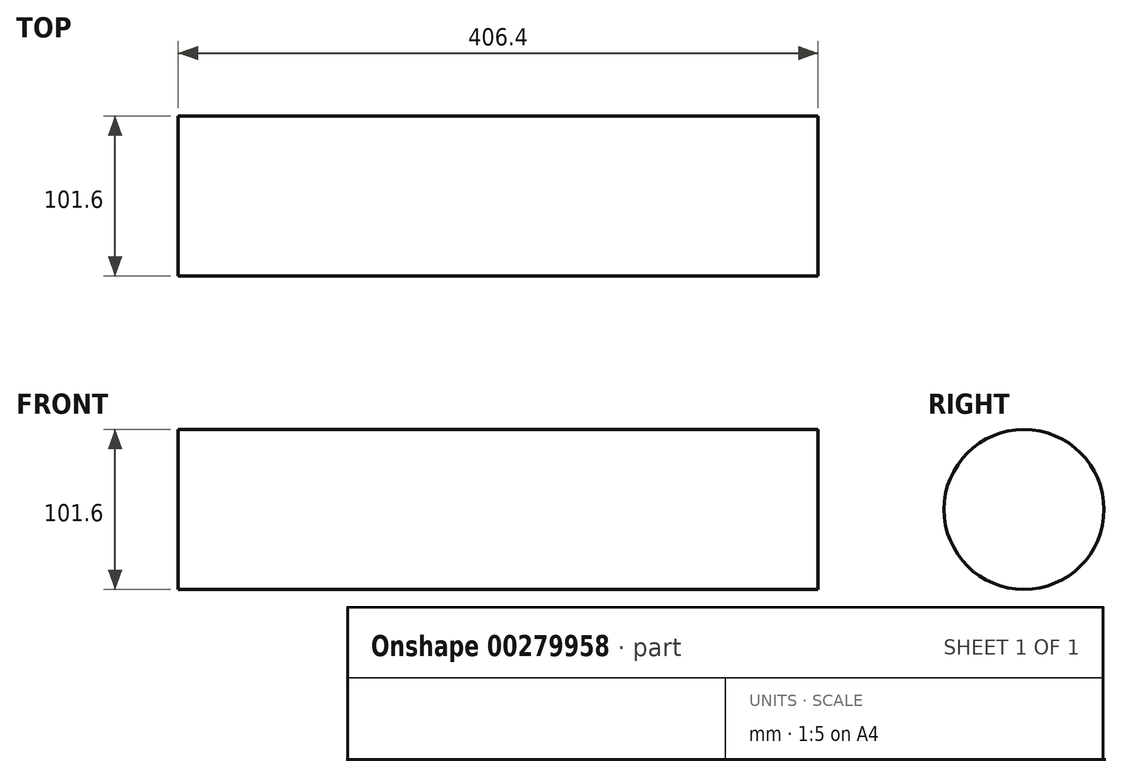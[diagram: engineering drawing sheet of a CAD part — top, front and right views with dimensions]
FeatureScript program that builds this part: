
annotation { "Feature Type Name" : "Feature", "Feature Type Description" : "" }
export const myFeature = defineFeature(function(context is Context, id is Id, definition is map)
    precondition{}
    {
        {
            var Q0;
            Q0=qCreatedBy(makeId("Right.planeOp"),FACE);
            var sketch = newSketch(context, id + "F0", { "sketchPlane" : qUnion([Q0])});
            skCircle(sketch, "E0", {"center": v(0, 0) * mm, "radius": 50.8 * mm});
            skSolve(sketch);
        }
        {
            var Q0;
            Q0=makeQuery(id+"F0.imprint","IMPRINT",FACE,{"disambiguationData":[TD([[makeQuery(id+"F0.imprint","IMPRINT",EDGE,{"derivedFrom":sQuery(id+"F0.wireOp",EDGE,"E0")}),1.0]])]});
            extrude(context, id + "F1", {"entities" : qUnion([Q0]), "endBound" : BoundingType.SYMMETRIC, "depth" : 406.4 * mm});
        }
    });
